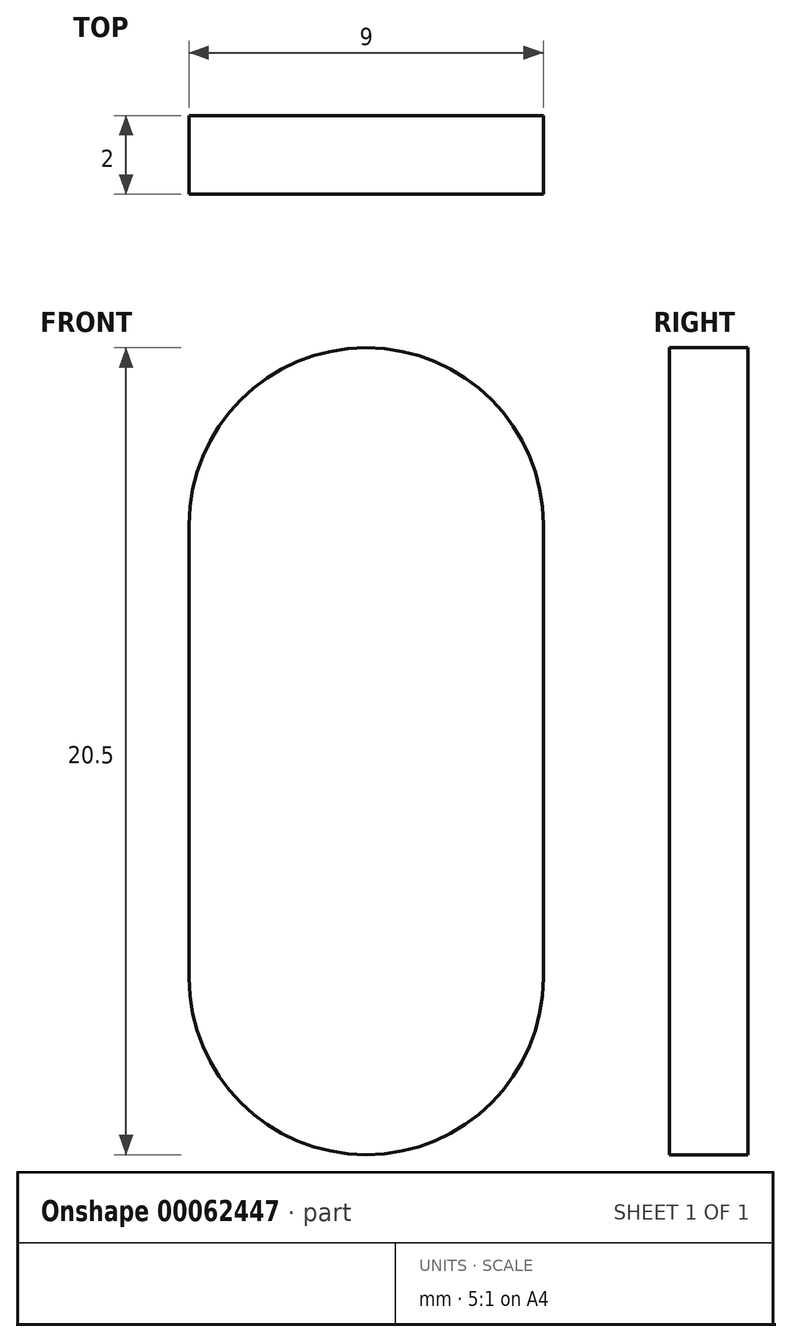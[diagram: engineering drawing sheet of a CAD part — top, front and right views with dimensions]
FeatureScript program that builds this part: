
annotation { "Feature Type Name" : "Feature", "Feature Type Description" : "" }
export const myFeature = defineFeature(function(context is Context, id is Id, definition is map)
    precondition{}
    {
        {
            var Q0;
            Q0=qCreatedBy(makeId("Front.planeOp"),FACE);
            var sketch = newSketch(context, id + "F0", { "sketchPlane" : qUnion([Q0])});
            skLineSegment(sketch, "E0.rect.bottom", {"start": v(4.5, -5.75) * mm, "end": v(-4.5, -5.75) * mm});
            skLineSegment(sketch, "E0.rect.top", {"start": v(4.5, 5.75) * mm, "end": v(-4.5, 5.75) * mm});
            skLineSegment(sketch, "E0.rect.left", {"start": v(4.5, -5.75) * mm, "end": v(4.5, 5.75) * mm});
            skLineSegment(sketch, "E0.rect.right", {"start": v(-4.5, -5.75) * mm, "end": v(-4.5, 5.75) * mm});
            skPoint(sketch, "E0.rect.middle", {"position": v(0, 0) * mm});
            skCircle(sketch, "E1", {"center": v(0, 5.75) * mm, "radius": 4.5 * mm});
            skCircle(sketch, "E2", {"center": v(0, -5.75) * mm, "radius": 4.5 * mm});
            skSolve(sketch);
        }
        {
            var Q0;
            Q0 = qSketchRegion(id + "F0", true);
            extrude(context, id + "F1", {"entities" : qUnion([Q0]), "depth" : 2 * mm});
        }
    });
